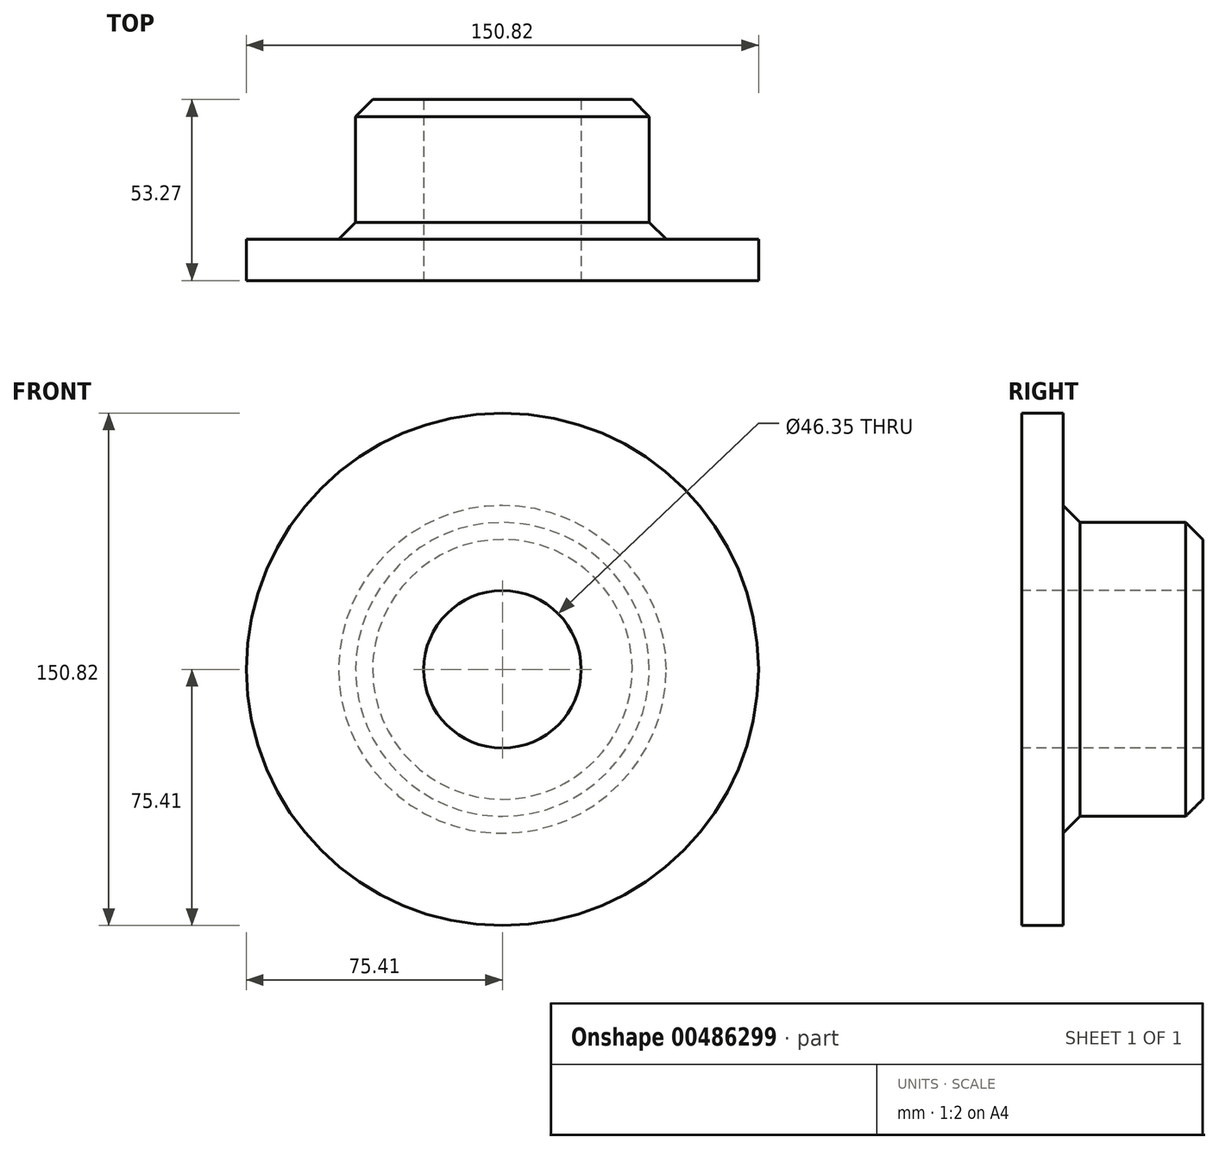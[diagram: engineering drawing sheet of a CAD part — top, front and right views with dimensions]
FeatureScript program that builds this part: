
annotation { "Feature Type Name" : "Feature", "Feature Type Description" : "" }
export const myFeature = defineFeature(function(context is Context, id is Id, definition is map)
    precondition{}
    {
        {
            var Q0;
            Q0=qCreatedBy(makeId("Right.planeOp"),FACE);
            var sketch = newSketch(context, id + "F0", { "sketchPlane" : qUnion([Q0])});
            skLineSegment(sketch, "E0", {"start": v(0, 0) * mm, "end": v(53.27, 0) * mm, "construction": true});
            skLineSegment(sketch, "E1.bottom", {"start": v(0, 23.18) * mm, "end": v(12.1, 23.18) * mm, "construction": true});
            skLineSegment(sketch, "E1.top", {"start": v(0, 75.4) * mm, "end": v(12.1, 75.4) * mm});
            skLineSegment(sketch, "E1.left", {"start": v(0, 23.18) * mm, "end": v(0, 75.4) * mm});
            skLineSegment(sketch, "E1.right", {"start": v(12.1, 23.18) * mm, "end": v(12.1, 75.4) * mm});
            skLineSegment(sketch, "E2.bottom", {"start": v(0, 23.18) * mm, "end": v(53.27, 23.18) * mm});
            skLineSegment(sketch, "E2.top", {"start": v(0, 43.24) * mm, "end": v(53.27, 43.24) * mm});
            skLineSegment(sketch, "E2.left", {"start": v(0, 23.18) * mm, "end": v(0, 43.24) * mm, "construction": true});
            skLineSegment(sketch, "E2.right", {"start": v(53.27, 23.18) * mm, "end": v(53.27, 43.24) * mm});
            skLineSegment(sketch, "E3.MirrorCS", {"start": v(0, -23.18) * mm, "end": v(12.1, -23.18) * mm, "construction": true});
            skLineSegment(sketch, "E4.MirrorCS", {"start": v(0, -23.18) * mm, "end": v(0, -43.24) * mm, "construction": true});
            skLineSegment(sketch, "E5.MirrorCS", {"start": v(0, -43.24) * mm, "end": v(53.27, -43.24) * mm});
            skLineSegment(sketch, "E6.MirrorCS", {"start": v(53.27, -23.18) * mm, "end": v(53.27, -43.24) * mm});
            skLineSegment(sketch, "E7.MirrorCS", {"start": v(12.1, -23.18) * mm, "end": v(12.1, -75.4) * mm});
            skLineSegment(sketch, "E8.MirrorCS", {"start": v(0, -23.18) * mm, "end": v(53.27, -23.18) * mm});
            skLineSegment(sketch, "E9.MirrorCS", {"start": v(0, -23.18) * mm, "end": v(0, -75.4) * mm});
            skLineSegment(sketch, "E10.MirrorCS", {"start": v(0, -75.4) * mm, "end": v(12.1, -75.4) * mm});
            skSolve(sketch);
        }
        {
            var Q0;
            {var subQ0=sQuery(id+"F0.wireOp",EDGE,"E1.top");Q0=makeQuery(id+"F0.imprint","IMPRINT",FACE,{"disambiguationData":[TD([[makeQuery(id+"F0.imprint","IMPRINT",EDGE,{"derivedFrom":subQ0}),-1.0]])]});}
            var Q1;
            {var subQ0=sQuery(id+"F0.wireOp",EDGE,"E2.bottom");var subQ1=sQuery(id+"F0.wireOp",EDGE,"E1.left");var subQ2=makeQuery(id+"F0.imprint","INTERSECT",VERTEX,{"derivedFrom":[subQ1,subQ0]});Q1=makeQuery(id+"F0.imprint","IMPRINT",FACE,{"disambiguationData":[TD([[makeQuery(id+"F0.imprint","IMPRINT",EDGE,{"disambiguationData":[TD([[subQ2,-1.0]])],"derivedFrom":subQ1}),-1.0]])]});}
            var Q2;
            {var subQ5=sQuery(id+"F0.wireOp",EDGE,"E2.right");Q2=makeQuery(id+"F0.imprint","IMPRINT",FACE,{"disambiguationData":[TD([[makeQuery(id+"F0.imprint","IMPRINT",EDGE,{"derivedFrom":subQ5}),1.0]])]});}
            var Q3;
            Q3=sQuery(id+"F0.wireOp",EDGE,"E0");
            revolve(context, id + "F1", {"entities" : qUnion([Q0, Q1, Q2]), "axis" : qUnion([Q3]), "revolveType" : RevolveType.FULL});
        }
        {
            var Q0;
            Q0=makeQuery(id+"F1.opRevolve","SWEPT_EDGE",EDGE,{"disambiguationData":[OSD([sQuery(id+"F0.wireOp",EDGE,"E1.right"),sQuery(id+"F0.wireOp",EDGE,"E2.top")])]});
            var Q1;
            Q1=makeQuery(id+"F1.opRevolve","SWEPT_EDGE",EDGE,{"disambiguationData":[OSD([sQuery(id+"F0.wireOp",EDGE,"E2.top"),sQuery(id+"F0.wireOp",EDGE,"E2.right")])]});
            chamfer(context, id + "F2", {"entities" : qUnion([Q0, Q1]), "width" : 5 * mm, "tangentPropagation" : true});
        }
    });
